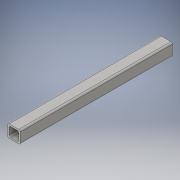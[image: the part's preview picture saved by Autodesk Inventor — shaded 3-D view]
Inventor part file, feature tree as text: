
AUTODESK INVENTOR PART (.ipt)
format: ipt  version: 2016 (Build 200138000, 138)  size: 112,128 bytes
history: native  units: in
note: dims shown in document units (in); Inventor stores cm internally (conversion verified against a paired STEP export)
features: extrude x1, sketch x1
ambient origin geometry x8: Origin, YZ Plane, XZ Plane, XY Plane, X Axis, Y Axis, Z Axis, Center Point
bodies: Solid1 (feature_tree)
feature tree (2):
  extrude  "Extrusion1"  Depth=1.0in
  sketch  "Sketch1"  dims[d0=1.0in d1=1.0in d2=0.125in d3=0.125in d4=12.0in d5=0.0in]
